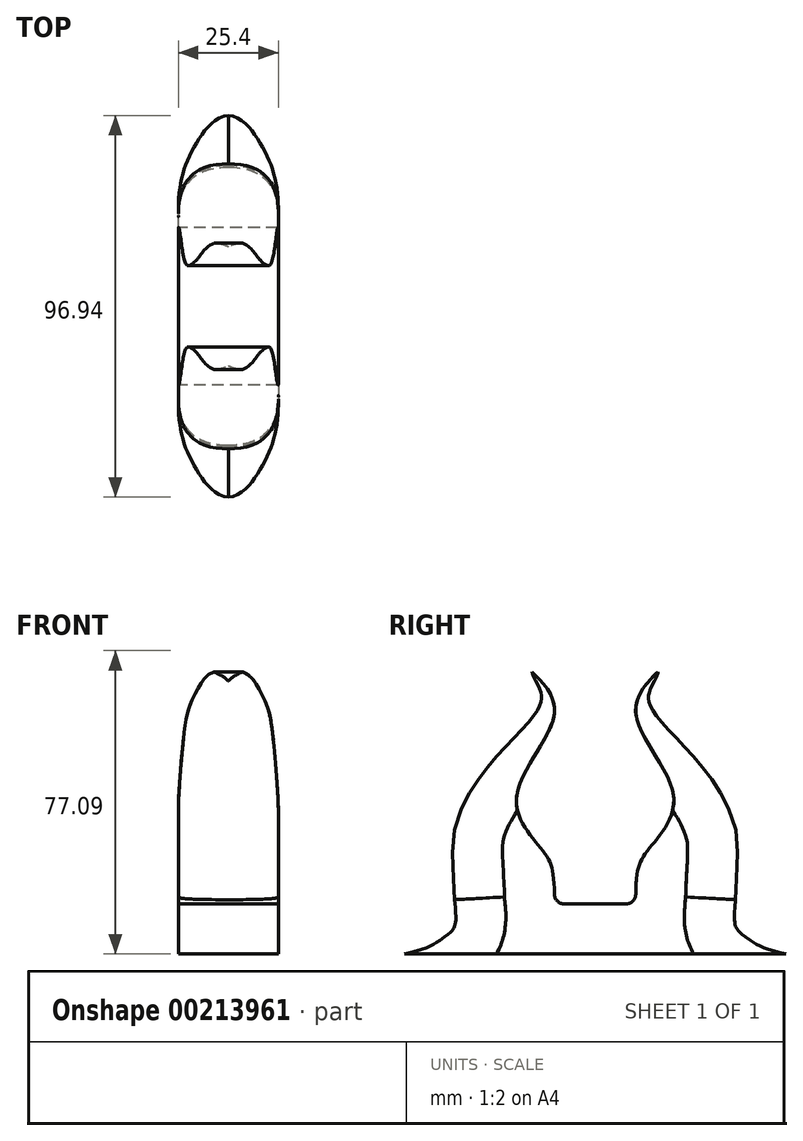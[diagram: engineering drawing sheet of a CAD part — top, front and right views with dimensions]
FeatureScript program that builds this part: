
annotation { "Feature Type Name" : "Feature", "Feature Type Description" : "" }
export const myFeature = defineFeature(function(context is Context, id is Id, definition is map)
    precondition{}
    {
        {
            var Q0;
            Q0=qCreatedBy(makeId("Right.planeOp"),FACE);
            var sketch = newSketch(context, id + "F0", { "sketchPlane" : qUnion([Q0])});
            skCircle(sketch, "E0", {"center": v(-23.02, 0) * mm, "radius": 12.7 * mm, "construction": true});
            skLineSegment(sketch, "E1", {"start": v(-10.32, -1.09) * mm, "end": v(-10.32, 59.8) * mm, "construction": true});
            skFitSpline(sketch, "E2", {"points": [v(-10.32, -1.09) * mm, v(-13.1, 12.17) * mm, v(-20, 25.82) * mm, v(-10.32, 47.52) * mm, v(-14.58, 56.49) * mm, v(-16, 57.9) * mm], "startDerivative": vector(0, 113.18) * mm, "endDerivative": vector(-13.07, 10.67) * mm});
            skFitSpline(sketch, "E3", {"points": [v(-35.72, 0) * mm, v(-35.72, 17.89) * mm, v(-26.74, 34.35) * mm, v(-14.76, 47.97) * mm, v(-13.87, 53.06) * mm, v(-16, 57.9) * mm], "startDerivative": vector(-1.1, 96.48) * mm, "endDerivative": vector(-3.2, 31.43) * mm});
            skFitSpline(sketch, "E4", {"points": [v(-35.72, 0) * mm, v(-35.72, -6.72) * mm, v(-38.34, -9.55) * mm, v(-41.91, -11.78) * mm, v(-48.47, -13.79) * mm], "startDerivative": vector(2.4, -26.4) * mm, "endDerivative": vector(-11.35, -1.33) * mm});
            skLineSegment(sketch, "E5", {"start": v(-48.47, -13.79) * mm, "end": v(0, -13.79) * mm});
            skLineSegment(sketch, "E6", {"start": v(-10.32, -1.09) * mm, "end": v(0, -1.09) * mm});
            skLineSegment(sketch, "E7", {"start": v(0, -13.79) * mm, "end": v(0, -1.09) * mm});
            skLineSegment(sketch, "E8.MirrorCS", {"start": v(48.47, -13.79) * mm, "end": v(0, -13.79) * mm});
            skFitSpline(sketch, "E9.MirrorCS", {"points": [v(35.72, 0) * mm, v(35.72, -6.72) * mm, v(38.34, -9.55) * mm, v(41.91, -11.78) * mm, v(48.47, -13.79) * mm], "startDerivative": vector(-2.4, -26.4) * mm, "endDerivative": vector(11.35, -1.33) * mm});
            skFitSpline(sketch, "E10.MirrorCS", {"points": [v(10.32, -1.09) * mm, v(13.1, 12.17) * mm, v(20, 25.82) * mm, v(10.32, 47.52) * mm, v(14.58, 56.49) * mm, v(16, 57.9) * mm], "startDerivative": vector(0, 113.18) * mm, "endDerivative": vector(13.07, 10.67) * mm});
            skCircle(sketch, "E11.MirrorC", {"center": v(23.02, 0) * mm, "radius": 12.7 * mm, "construction": true});
            skLineSegment(sketch, "E12.MirrorCS", {"start": v(10.32, -1.09) * mm, "end": v(10.32, 59.8) * mm, "construction": true});
            skLineSegment(sketch, "E13.MirrorCS", {"start": v(10.32, -1.09) * mm, "end": v(0, -1.09) * mm});
            skFitSpline(sketch, "E14.MirrorCS", {"points": [v(35.72, 0) * mm, v(35.72, 17.89) * mm, v(26.74, 34.35) * mm, v(14.76, 47.97) * mm, v(13.87, 53.06) * mm, v(16, 57.9) * mm], "startDerivative": vector(1.1, 96.48) * mm, "endDerivative": vector(3.2, 31.43) * mm});
            skSolve(sketch);
        }
        {
            var Q0;
            Q0 = qSketchRegion(id + "F0", true);
            extrude(context, id + "F1", {"entities" : qUnion([Q0]), "depth" : 25.4 * mm});
        }
        {
            var Q0;
            Q0=makeQuery(id+"F1.opExtrude","CAP_EDGE",EDGE,{"disambiguationData":[OSD([sQuery(id+"F0.wireOp",EDGE,"E3")])],"isStart":false});
            var Q1;
            Q1=makeQuery(id+"F1.opExtrude","CAP_EDGE",EDGE,{"disambiguationData":[OSD([sQuery(id+"F0.wireOp",EDGE,"E4")])],"isStart":false});
            var Q2;
            Q2=makeQuery(id+"F1.opExtrude","CAP_EDGE",EDGE,{"disambiguationData":[OSD([sQuery(id+"F0.wireOp",EDGE,"E4")])],"isStart":true});
            var Q3;
            Q3=makeQuery(id+"F1.opExtrude","CAP_EDGE",EDGE,{"disambiguationData":[OSD([sQuery(id+"F0.wireOp",EDGE,"E3")])],"isStart":true});
            var Q4;
            Q4=makeQuery(id+"F1.opExtrude","CAP_EDGE",EDGE,{"disambiguationData":[OSD([sQuery(id+"F0.wireOp",EDGE,"E14.MirrorCS")])],"isStart":false});
            var Q5;
            Q5=makeQuery(id+"F1.opExtrude","CAP_EDGE",EDGE,{"disambiguationData":[OSD([sQuery(id+"F0.wireOp",EDGE,"E14.MirrorCS")])],"isStart":true});
            var Q6;
            Q6=makeQuery(id+"F1.opExtrude","CAP_EDGE",EDGE,{"disambiguationData":[OSD([sQuery(id+"F0.wireOp",EDGE,"E9.MirrorCS")])],"isStart":false});
            var Q7;
            Q7=makeQuery(id+"F1.opExtrude","CAP_EDGE",EDGE,{"disambiguationData":[OSD([sQuery(id+"F0.wireOp",EDGE,"E9.MirrorCS")])],"isStart":true});
            fillet(context, id + "F2", {"entities" : qUnion([Q0, Q1, Q2, Q3, Q4, Q5, Q6, Q7]), "radius" : 12.7 * mm, "tangentPropagation" : true, "rho" : 0.5, "crossSection" : FilletCrossSection.CONIC, "allowEdgeOverflow" : false});
        }
        {
            var Q0;
            Q0=makeQuery(id+"F1.opExtrude","SWEPT_EDGE",EDGE,{"disambiguationData":[OSD([sQuery(id+"F0.wireOp",EDGE,"E10.MirrorCS"),sQuery(id+"F0.wireOp",EDGE,"E13.MirrorCS")])]});
            var Q1;
            Q1=makeQuery(id+"F1.opExtrude","SWEPT_EDGE",EDGE,{"disambiguationData":[OSD([sQuery(id+"F0.wireOp",EDGE,"E2"),sQuery(id+"F0.wireOp",EDGE,"E6")])]});
            fillet(context, id + "F3", {"entities" : qUnion([Q0, Q1]), "radius" : 2.54 * mm, "tangentPropagation" : true, "allowEdgeOverflow" : false});
        }
    });
